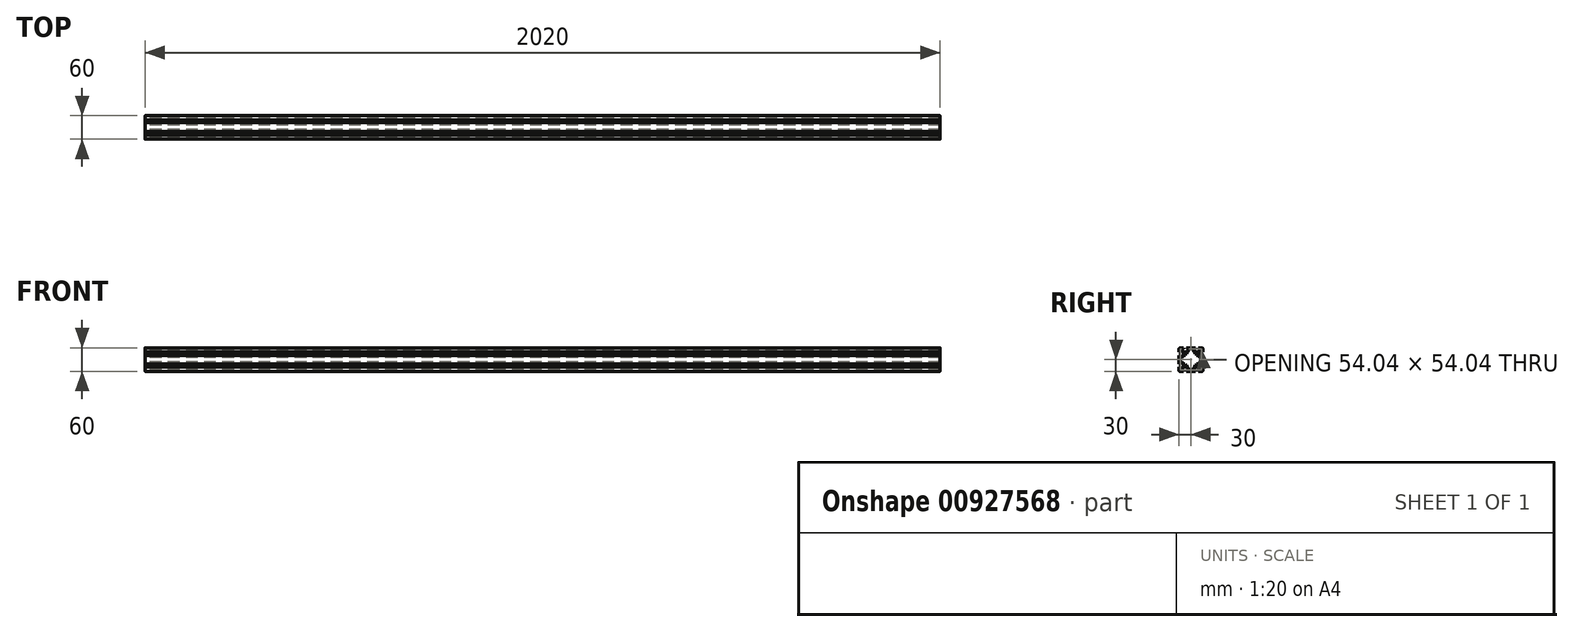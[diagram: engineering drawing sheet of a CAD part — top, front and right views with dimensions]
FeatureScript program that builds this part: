
annotation { "Feature Type Name" : "Feature", "Feature Type Description" : "" }
export const myFeature = defineFeature(function(context is Context, id is Id, definition is map)
    precondition{}
    {
        {
            var Q0;
            Q0=qCreatedBy(makeId("Right.planeOp"),FACE);
            var sketch = newSketch(context, id + "F0", { "sketchPlane" : qUnion([Q0])});
            skLineSegment(sketch, "E0", {"start": v(15, 43.7) * mm, "end": v(15, -35.2) * mm, "construction": true});
            skLineSegment(sketch, "E1.MirrorCS", {"start": v(-15, 43.7) * mm, "end": v(-15, -35.2) * mm, "construction": true});
            skLineSegment(sketch, "E2.MirrorCS", {"start": v(-40.74, -15) * mm, "end": v(50.74, -15) * mm, "construction": true});
            skLineSegment(sketch, "E3.0", {"start": v(30, 30) * mm, "end": v(30, 19.02) * mm});
            skLineSegment(sketch, "E4.MirrorCS", {"start": v(-30, 30) * mm, "end": v(-30, 19) * mm});
            skLineSegment(sketch, "E5.0", {"start": v(-30, -30) * mm, "end": v(-19, -30) * mm});
            skLineSegment(sketch, "E6.MirrorCS", {"start": v(-30, 30) * mm, "end": v(-19, 30) * mm});
            skPoint(sketch, "E7", {"position": v(-15, 15) * mm});
            skPoint(sketch, "E8", {"position": v(15, 15) * mm});
            skPoint(sketch, "E9", {"position": v(15, -15) * mm});
            skPoint(sketch, "E10", {"position": v(-15, -15) * mm});
            skArc(sketch, "E11", {"start": v(-11.75, 14) * mm, "mid": v(-17.4, 17.4) * mm, "end": v(-14, 11.75) * mm});
            skArc(sketch, "E12", {"start": v(14, 11.75) * mm, "mid": v(17.4, 17.4) * mm, "end": v(11.75, 14) * mm});
            skArc(sketch, "E13", {"start": v(-14.71, -11.61) * mm, "mid": v(-17.13, -17.65) * mm, "end": v(-11.75, -14) * mm});
            skArc(sketch, "E14", {"start": v(11.75, -14) * mm, "mid": v(17.4, -17.4) * mm, "end": v(14, -11.75) * mm});
            skLineSegment(sketch, "E15", {"start": v(-19, 30) * mm, "end": v(-19, 27.09) * mm});
            skLineSegment(sketch, "E16", {"start": v(-30, 19) * mm, "end": v(-27.09, 19) * mm});
            skLineSegment(sketch, "E17", {"start": v(-19, 27.09) * mm, "end": v(-22.31, 27.09) * mm});
            skLineSegment(sketch, "E18", {"start": v(-27.09, 19) * mm, "end": v(-27.09, 23.27) * mm});
            skLineSegment(sketch, "E19", {"start": v(-24.34, 23.27) * mm, "end": v(-19.39, 17.97) * mm});
            skLineSegment(sketch, "E20.MirrorCS", {"start": v(-22.31, 24.03) * mm, "end": v(-17.97, 19.39) * mm});
            skLineSegment(sketch, "E21", {"start": v(-27.09, 23.27) * mm, "end": v(-24.34, 23.27) * mm});
            skLineSegment(sketch, "E22", {"start": v(-22.31, 24.03) * mm, "end": v(-22.31, 27.09) * mm});
            skLineSegment(sketch, "E23", {"start": v(-11, 30) * mm, "end": v(-11, 28) * mm});
            skLineSegment(sketch, "E24", {"start": v(11.94, 30) * mm, "end": v(11.94, 27.95) * mm});
            skLineSegment(sketch, "E25", {"start": v(11.94, 27.95) * mm, "end": v(7.69, 27.95) * mm});
            skLineSegment(sketch, "E26", {"start": v(-11, 28) * mm, "end": v(-7.69, 28) * mm});
            skLineSegment(sketch, "E27.trimOffspring", {"start": v(-11, 30) * mm, "end": v(11.94, 30) * mm});
            skLineSegment(sketch, "E28.MirrorCS", {"start": v(22.31, 24.03) * mm, "end": v(17.97, 19.39) * mm});
            skLineSegment(sketch, "E29.MirrorCS", {"start": v(24.34, 23.27) * mm, "end": v(19.39, 17.97) * mm});
            skLineSegment(sketch, "E30", {"start": v(19, 30) * mm, "end": v(19, 27.09) * mm});
            skLineSegment(sketch, "E31", {"start": v(30, 19.02) * mm, "end": v(27.09, 19.02) * mm});
            skLineSegment(sketch, "E32", {"start": v(27.09, 19.02) * mm, "end": v(27.09, 23.27) * mm});
            skLineSegment(sketch, "E33", {"start": v(24.34, 23.27) * mm, "end": v(27.09, 23.27) * mm});
            skLineSegment(sketch, "E34", {"start": v(17.97, 19.39) * mm, "end": v(14.2, 19.39) * mm});
            skLineSegment(sketch, "E35", {"start": v(19.39, 17.97) * mm, "end": v(19.39, 11.88) * mm});
            skLineSegment(sketch, "E36", {"start": v(-5.66, 27.02) * mm, "end": v(-5.66, 23.27) * mm});
            skLineSegment(sketch, "E37.MirrorCS", {"start": v(-7.69, 24.03) * mm, "end": v(-12.03, 19.39) * mm});
            skLineSegment(sketch, "E38.MirrorCS", {"start": v(-5.66, 23.27) * mm, "end": v(-10.61, 17.97) * mm});
            skLineSegment(sketch, "E39", {"start": v(-10.61, 17.97) * mm, "end": v(-10.61, 14) * mm});
            skLineSegment(sketch, "E40.MirrorCS", {"start": v(10.61, 17.97) * mm, "end": v(10.61, 14) * mm});
            skLineSegment(sketch, "E41.MirrorCS", {"start": v(5.66, 23.27) * mm, "end": v(10.61, 17.97) * mm});
            skLineSegment(sketch, "E42.MirrorCS", {"start": v(7.69, 24.03) * mm, "end": v(12.03, 19.39) * mm});
            skLineSegment(sketch, "E43.MirrorCS", {"start": v(5.66, 27.02) * mm, "end": v(5.66, 23.27) * mm});
            skLineSegment(sketch, "E44", {"start": v(7.69, 24.03) * mm, "end": v(7.69, 26.95) * mm});
            skLineSegment(sketch, "E45", {"start": v(-5.66, 27.02) * mm, "end": v(5.66, 27.02) * mm});
            skLineSegment(sketch, "E46.trimOffspring", {"start": v(19, 30) * mm, "end": v(30, 30) * mm});
            skLineSegment(sketch, "E47", {"start": v(-7.69, 28) * mm, "end": v(-7.69, 24.03) * mm});
            skLineSegment(sketch, "E48", {"start": v(12.03, 19.39) * mm, "end": v(14.2, 19.39) * mm});
            skLineSegment(sketch, "E49", {"start": v(22.31, 27.09) * mm, "end": v(22.31, 24.03) * mm});
            skLineSegment(sketch, "E50", {"start": v(19, 27.09) * mm, "end": v(22.31, 27.09) * mm});
            skLineSegment(sketch, "E51", {"start": v(7.69, 26.95) * mm, "end": v(7.69, 27.95) * mm});
            skLineSegment(sketch, "E52.MirrorCS", {"start": v(-27.09, -19) * mm, "end": v(-27.09, -23.27) * mm});
            skLineSegment(sketch, "E53.MirrorCS", {"start": v(-27.09, -23.27) * mm, "end": v(-24.34, -23.27) * mm});
            skLineSegment(sketch, "E54.MirrorCS", {"start": v(-24.34, -23.27) * mm, "end": v(-19.39, -17.97) * mm});
            skLineSegment(sketch, "E55.MirrorCS", {"start": v(-19, -30) * mm, "end": v(-19, -27.09) * mm});
            skLineSegment(sketch, "E56.MirrorCS", {"start": v(-19, -27.09) * mm, "end": v(-22.31, -27.09) * mm});
            skLineSegment(sketch, "E57.MirrorCS", {"start": v(-22.31, -24.03) * mm, "end": v(-22.31, -27.09) * mm});
            skLineSegment(sketch, "E58.MirrorCS", {"start": v(-22.31, -24.03) * mm, "end": v(-17.97, -19.39) * mm});
            skLineSegment(sketch, "E59.MirrorCS", {"start": v(-17.97, -19.39) * mm, "end": v(-7.8, -19.39) * mm});
            skLineSegment(sketch, "E60.MirrorCS", {"start": v(-17.97, -19.39) * mm, "end": v(-12.03, -19.39) * mm});
            skLineSegment(sketch, "E61.MirrorCS", {"start": v(-7.69, -24.03) * mm, "end": v(-12.03, -19.39) * mm});
            skLineSegment(sketch, "E62.MirrorCS", {"start": v(-7.69, -28) * mm, "end": v(-7.69, -24.03) * mm});
            skLineSegment(sketch, "E63.MirrorCS", {"start": v(-11, -28) * mm, "end": v(-7.69, -28) * mm});
            skLineSegment(sketch, "E64.MirrorCS", {"start": v(-11, -30) * mm, "end": v(-11, -28) * mm});
            skLineSegment(sketch, "E65.MirrorCS", {"start": v(-11, -30) * mm, "end": v(11.94, -30) * mm});
            skLineSegment(sketch, "E66.MirrorCS", {"start": v(11.94, -30) * mm, "end": v(11.94, -27.95) * mm});
            skLineSegment(sketch, "E67.MirrorCS", {"start": v(11.94, -27.95) * mm, "end": v(7.69, -27.95) * mm});
            skLineSegment(sketch, "E68.MirrorCS", {"start": v(5.66, -27.02) * mm, "end": v(5.66, -23.27) * mm});
            skLineSegment(sketch, "E69.MirrorCS", {"start": v(5.66, -23.27) * mm, "end": v(10.61, -17.97) * mm});
            skLineSegment(sketch, "E70.MirrorCS", {"start": v(10.61, -17.97) * mm, "end": v(10.61, -14) * mm});
            skLineSegment(sketch, "E71.MirrorCS", {"start": v(7.69, -26.95) * mm, "end": v(7.69, -27.95) * mm});
            skLineSegment(sketch, "E72.MirrorCS", {"start": v(7.69, -24.03) * mm, "end": v(7.69, -26.95) * mm});
            skLineSegment(sketch, "E73.MirrorCS", {"start": v(7.69, -24.03) * mm, "end": v(12.03, -19.39) * mm});
            skLineSegment(sketch, "E74.MirrorCS", {"start": v(12.03, -19.39) * mm, "end": v(14.2, -19.39) * mm});
            skLineSegment(sketch, "E75.MirrorCS", {"start": v(-5.66, -27.02) * mm, "end": v(5.66, -27.02) * mm});
            skLineSegment(sketch, "E76.MirrorCS", {"start": v(-5.66, -27.02) * mm, "end": v(-5.66, -23.27) * mm});
            skLineSegment(sketch, "E77.MirrorCS", {"start": v(-5.66, -23.27) * mm, "end": v(-10.61, -17.97) * mm});
            skLineSegment(sketch, "E78.MirrorCS", {"start": v(-10.61, -17.97) * mm, "end": v(-10.61, -14) * mm});
            skLineSegment(sketch, "E79.MirrorCS", {"start": v(17.97, -19.39) * mm, "end": v(14.2, -19.39) * mm});
            skLineSegment(sketch, "E80.MirrorCS", {"start": v(22.31, -24.03) * mm, "end": v(17.97, -19.39) * mm});
            skLineSegment(sketch, "E81.MirrorCS", {"start": v(22.31, -27.09) * mm, "end": v(22.31, -24.03) * mm});
            skLineSegment(sketch, "E82.MirrorCS", {"start": v(19, -27.09) * mm, "end": v(22.31, -27.09) * mm});
            skLineSegment(sketch, "E83.MirrorCS", {"start": v(19, -30) * mm, "end": v(19, -27.09) * mm});
            skLineSegment(sketch, "E84.MirrorCS", {"start": v(19, -30) * mm, "end": v(30, -30) * mm});
            skLineSegment(sketch, "E85.MirrorCS", {"start": v(30, -19.02) * mm, "end": v(27.09, -19.02) * mm});
            skLineSegment(sketch, "E86.MirrorCS", {"start": v(27.09, -19.02) * mm, "end": v(27.09, -23.27) * mm});
            skLineSegment(sketch, "E87.MirrorCS", {"start": v(24.34, -23.27) * mm, "end": v(27.09, -23.27) * mm});
            skLineSegment(sketch, "E88.MirrorCS", {"start": v(24.34, -23.27) * mm, "end": v(19.39, -17.97) * mm});
            skLineSegment(sketch, "E89.MirrorCS", {"start": v(19.39, -17.97) * mm, "end": v(19.39, -11.88) * mm});
            skLineSegment(sketch, "E90", {"start": v(-30, 30) * mm, "end": v(30, -30) * mm, "construction": true});
            skLineSegment(sketch, "E91.MirrorCS", {"start": v(-30, 11) * mm, "end": v(-28, 11) * mm});
            skLineSegment(sketch, "E92.MirrorCS", {"start": v(-28, 11) * mm, "end": v(-28, 7.69) * mm});
            skLineSegment(sketch, "E93.MirrorCS", {"start": v(-28, 7.69) * mm, "end": v(-24.03, 7.69) * mm});
            skLineSegment(sketch, "E94", {"start": v(30, 30) * mm, "end": v(-30, -30) * mm, "construction": true});
            skLineSegment(sketch, "E95.MirrorCS", {"start": v(-30, -19) * mm, "end": v(-27.09, -19) * mm});
            skLineSegment(sketch, "E96.MirrorCS", {"start": v(-30, -11) * mm, "end": v(-28, -11) * mm});
            skLineSegment(sketch, "E97.MirrorCS", {"start": v(-28, -11) * mm, "end": v(-28, -7.69) * mm});
            skLineSegment(sketch, "E98.MirrorCS", {"start": v(-28, -7.69) * mm, "end": v(-24.03, -7.69) * mm});
            skLineSegment(sketch, "E99.MirrorCS", {"start": v(-24.03, -7.69) * mm, "end": v(-19.39, -12.03) * mm});
            skLineSegment(sketch, "E100.MirrorCS", {"start": v(-19.39, -17.97) * mm, "end": v(-19.39, -12.03) * mm});
            skLineSegment(sketch, "E101.MirrorCS", {"start": v(-27.02, -5.66) * mm, "end": v(-27.02, 5.66) * mm});
            skLineSegment(sketch, "E102.MirrorCS", {"start": v(-27.02, -5.66) * mm, "end": v(-23.27, -5.66) * mm});
            skLineSegment(sketch, "E103.MirrorCS", {"start": v(-23.27, -5.66) * mm, "end": v(-17.97, -10.61) * mm});
            skLineSegment(sketch, "E104.MirrorCS", {"start": v(-17.97, -10.61) * mm, "end": v(-14.71, -10.61) * mm});
            skLineSegment(sketch, "E105.MirrorCS", {"start": v(-23.27, 5.66) * mm, "end": v(-17.97, 10.61) * mm});
            skLineSegment(sketch, "E106", {"start": v(-17.97, 19.39) * mm, "end": v(-12.03, 19.39) * mm});
            skLineSegment(sketch, "E107.MirrorCS", {"start": v(-24.03, 7.69) * mm, "end": v(-19.39, 12.03) * mm});
            skLineSegment(sketch, "E108.MirrorCS", {"start": v(-17.97, 10.61) * mm, "end": v(-14, 10.61) * mm});
            skLineSegment(sketch, "E109", {"start": v(-19.39, 17.97) * mm, "end": v(-19.39, 12.03) * mm});
            skLineSegment(sketch, "E110", {"start": v(-27.02, 5.66) * mm, "end": v(-23.27, 5.66) * mm});
            skLineSegment(sketch, "E111.MirrorCS", {"start": v(27.02, -5.66) * mm, "end": v(27.02, 5.66) * mm});
            skLineSegment(sketch, "E112.MirrorCS", {"start": v(30, 11) * mm, "end": v(28, 11) * mm});
            skLineSegment(sketch, "E113.MirrorCS", {"start": v(28, 11) * mm, "end": v(28, 7.69) * mm});
            skLineSegment(sketch, "E114.MirrorCS", {"start": v(28, 7.69) * mm, "end": v(24.03, 7.69) * mm});
            skLineSegment(sketch, "E115.MirrorCS", {"start": v(23.27, 5.66) * mm, "end": v(17.97, 10.61) * mm});
            skLineSegment(sketch, "E116.MirrorCS", {"start": v(17.97, 10.61) * mm, "end": v(14, 10.61) * mm});
            skLineSegment(sketch, "E117.MirrorCS", {"start": v(27.02, 5.66) * mm, "end": v(23.27, 5.66) * mm});
            skLineSegment(sketch, "E118.MirrorCS", {"start": v(27.02, -5.66) * mm, "end": v(23.27, -5.66) * mm});
            skLineSegment(sketch, "E119.MirrorCS", {"start": v(23.27, -5.66) * mm, "end": v(17.97, -10.61) * mm});
            skLineSegment(sketch, "E120.MirrorCS", {"start": v(17.97, -10.61) * mm, "end": v(14, -10.61) * mm});
            skLineSegment(sketch, "E121.MirrorCS", {"start": v(30, -11) * mm, "end": v(28, -11) * mm});
            skLineSegment(sketch, "E122.MirrorCS", {"start": v(28, -11) * mm, "end": v(28, -7.69) * mm});
            skLineSegment(sketch, "E123.MirrorCS", {"start": v(28, -7.69) * mm, "end": v(24.03, -7.69) * mm});
            skLineSegment(sketch, "E124.MirrorCS", {"start": v(24.03, -7.69) * mm, "end": v(19.39, -12.03) * mm});
            skLineSegment(sketch, "E125.MirrorCS", {"start": v(24.03, 7.69) * mm, "end": v(19.39, 12.03) * mm});
            skLineSegment(sketch, "E126.trimOffspring", {"start": v(-30, -19) * mm, "end": v(-30, -30) * mm});
            skLineSegment(sketch, "E127.trimOffspring", {"start": v(30, -19.02) * mm, "end": v(30, -30) * mm});
            skLineSegment(sketch, "E128.trimOffspring", {"start": v(30, 11) * mm, "end": v(30, -11) * mm});
            skLineSegment(sketch, "E129.trimOffspring", {"start": v(-30, 11) * mm, "end": v(-30, -11) * mm});
            skLineSegment(sketch, "E130", {"start": v(-11.75, -14) * mm, "end": v(-10.61, -14) * mm});
            skLineSegment(sketch, "E131", {"start": v(-14.71, -10.61) * mm, "end": v(-14.71, -11.61) * mm});
            skLineSegment(sketch, "E132", {"start": v(-14, 10.61) * mm, "end": v(-14, 11.75) * mm});
            skLineSegment(sketch, "E133", {"start": v(-43.9, 15) * mm, "end": v(47.3, 15) * mm, "construction": true});
            skLineSegment(sketch, "E134", {"start": v(-11.75, 14) * mm, "end": v(-10.61, 14) * mm});
            skLineSegment(sketch, "E135", {"start": v(10.61, 14) * mm, "end": v(11.75, 14) * mm});
            skLineSegment(sketch, "E136", {"start": v(14, 11.75) * mm, "end": v(14, 10.61) * mm});
            skLineSegment(sketch, "E137", {"start": v(10.61, -14) * mm, "end": v(11.75, -14) * mm});
            skLineSegment(sketch, "E138", {"start": v(14, -10.61) * mm, "end": v(14, -11.75) * mm});
            skLineSegment(sketch, "E139", {"start": v(19.39, -11.88) * mm, "end": v(19.39, -12.03) * mm});
            skLineSegment(sketch, "E140", {"start": v(19.39, 12.03) * mm, "end": v(19.39, 11.88) * mm});
            skSolve(sketch);
        }
        {
            var Q0;
            Q0 = qSketchRegion(id + "F0", true);
            extrude(context, id + "F1", {"entities" : qUnion([Q0]), "depth" : 2020 * mm, "offsetDistance" : 25 * mm});
        }
        {
            var Q0;
            Q0=makeQuery(id+"F1.opExtrude","SWEPT_EDGE",EDGE,{"disambiguationData":[OSD([sQuery(id+"F0.wireOp",EDGE,"E4.MirrorCS"),sQuery(id+"F0.wireOp",EDGE,"E6.MirrorCS")])]});
            var Q1;
            Q1=makeQuery(id+"F1.opExtrude","SWEPT_EDGE",EDGE,{"disambiguationData":[OSD([sQuery(id+"F0.wireOp",EDGE,"E3.0"),sQuery(id+"F0.wireOp",EDGE,"E46.trimOffspring")])]});
            var Q2;
            Q2=makeQuery(id+"F1.opExtrude","SWEPT_EDGE",EDGE,{"disambiguationData":[OSD([sQuery(id+"F0.wireOp",EDGE,"E84.MirrorCS"),sQuery(id+"F0.wireOp",EDGE,"E127.trimOffspring")])]});
            var Q3;
            Q3=makeQuery(id+"F1.opExtrude","SWEPT_EDGE",EDGE,{"disambiguationData":[OSD([sQuery(id+"F0.wireOp",EDGE,"E5.0"),sQuery(id+"F0.wireOp",EDGE,"E126.trimOffspring")])]});
            fillet(context, id + "F2", {"entities" : qUnion([Q0, Q1, Q2, Q3]), "radius" : 2 * mm, "tangentPropagation" : true, "allowEdgeOverflow" : false});
        }
    });
